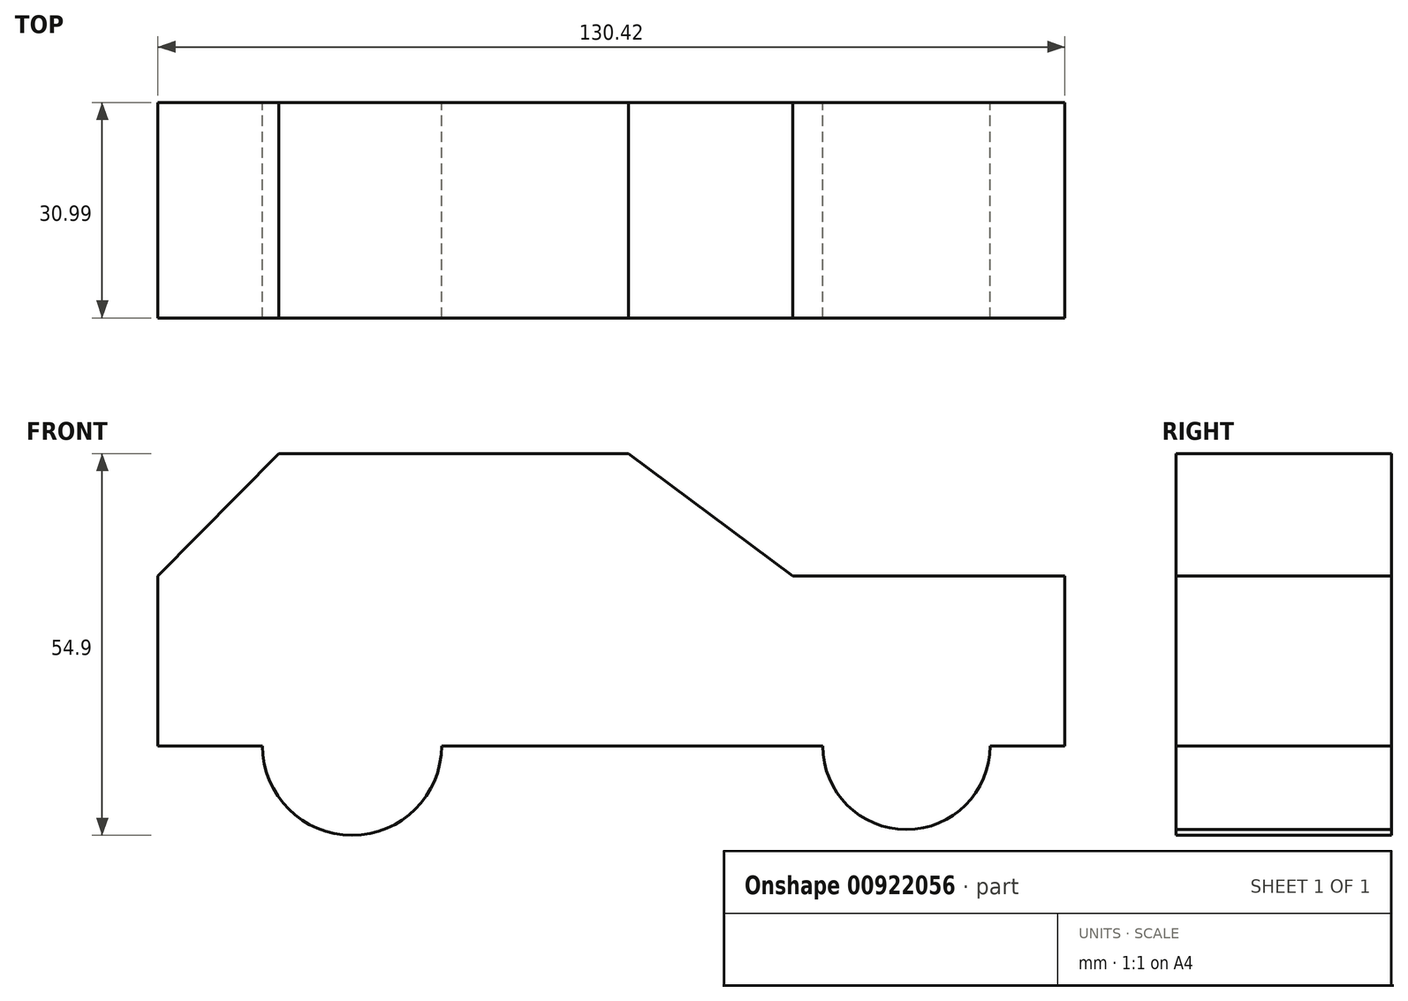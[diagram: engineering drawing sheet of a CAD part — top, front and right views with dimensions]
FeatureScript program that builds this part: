
annotation { "Feature Type Name" : "Feature", "Feature Type Description" : "" }
export const myFeature = defineFeature(function(context is Context, id is Id, definition is map)
    precondition{}
    {
        {
            var Q0;
            Q0=qCreatedBy(makeId("Front.planeOp"),FACE);
            var sketch = newSketch(context, id + "F0", { "sketchPlane" : qUnion([Q0])});
            skLineSegment(sketch, "E0", {"start": v(62.72, -17.62) * mm, "end": v(62.72, -42.03) * mm});
            skLineSegment(sketch, "E1", {"start": v(62.72, -17.62) * mm, "end": v(23.6, -17.62) * mm});
            skLineSegment(sketch, "E2", {"start": v(23.6, -17.62) * mm, "end": v(0, 0) * mm});
            skLineSegment(sketch, "E3", {"start": v(0, 0) * mm, "end": v(-50.3, 0) * mm});
            skLineSegment(sketch, "E4", {"start": v(-50.3, 0) * mm, "end": v(-67.7, -17.62) * mm});
            skLineSegment(sketch, "E5", {"start": v(-67.7, -17.62) * mm, "end": v(-67.7, -38.69) * mm});
            skLineSegment(sketch, "E6", {"start": v(62.72, -42.03) * mm, "end": v(62.72, -38.69) * mm});
            skLineSegment(sketch, "E7", {"start": v(-67.7, -38.69) * mm, "end": v(-67.7, -42.03) * mm});
            skLineSegment(sketch, "E8", {"start": v(-67.7, -42.03) * mm, "end": v(-52.65, -42.03) * mm});
            skLineSegment(sketch, "E9", {"start": v(-52.65, -42.03) * mm, "end": v(-26.91, -42.03) * mm, "construction": true});
            skLineSegment(sketch, "E10", {"start": v(-26.91, -42.03) * mm, "end": v(27.9, -42.03) * mm});
            skLineSegment(sketch, "E11", {"start": v(27.9, -42.03) * mm, "end": v(51.97, -42.03) * mm, "construction": true});
            skLineSegment(sketch, "E12", {"start": v(51.97, -42.03) * mm, "end": v(62.72, -42.03) * mm});
            skPoint(sketch, "E13", {"position": v(-39.78, -42.03) * mm});
            skPoint(sketch, "E14", {"position": v(39.93, -42.03) * mm});
            skArc(sketch, "E15", {"start": v(-26.91, -42.03) * mm, "mid": v(-39.78, -54.9) * mm, "end": v(-52.65, -42.03) * mm});
            skArc(sketch, "E16", {"start": v(51.97, -42.03) * mm, "mid": v(39.93, -54.06) * mm, "end": v(27.9, -42.03) * mm});
            skSolve(sketch);
        }
        {
            var Q0;
            Q0=makeQuery(id+"F0.imprint","IMPRINT",FACE,{"disambiguationData":[TD([[makeQuery(id+"F0.imprint","IMPRINT",EDGE,{"derivedFrom":sQuery(id+"F0.wireOp",EDGE,"E0")}),-1.0]])]});
            extrude(context, id + "F1", {"entities" : qUnion([Q0]), "depth" : 30.99 * mm, "offsetDistance" : 25.4 * mm});
        }
    });
